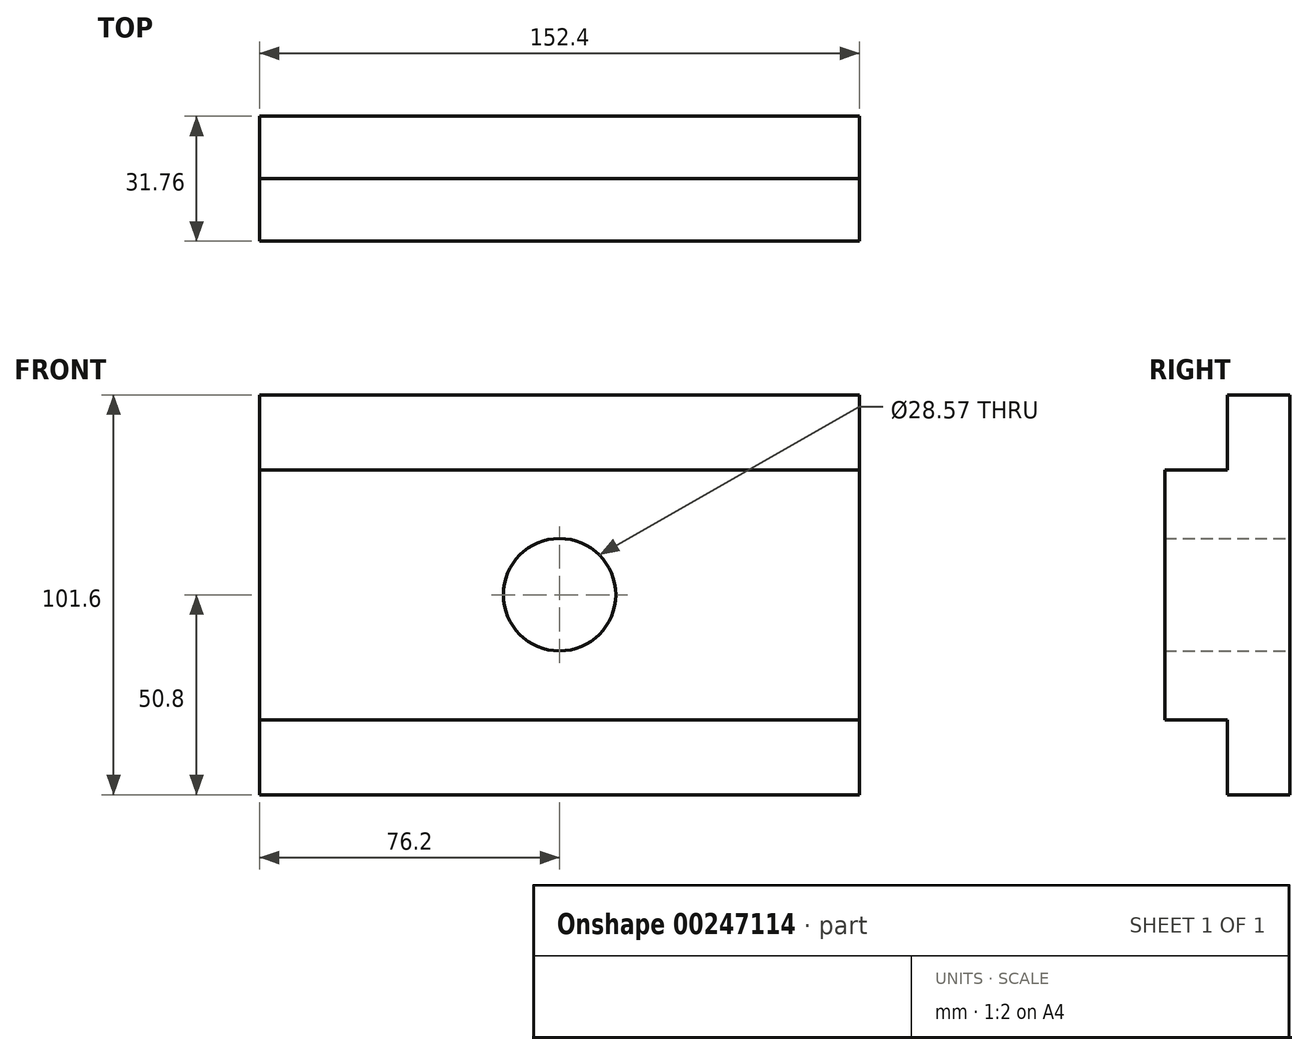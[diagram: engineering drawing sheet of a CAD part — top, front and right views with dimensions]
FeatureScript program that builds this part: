
annotation { "Feature Type Name" : "Feature", "Feature Type Description" : "" }
export const myFeature = defineFeature(function(context is Context, id is Id, definition is map)
    precondition{}
    {
        {
            var Q0;
            Q0=qCreatedBy(makeId("Front.planeOp"),FACE);
            var sketch = newSketch(context, id + "F0", { "sketchPlane" : qUnion([Q0])});
            skLineSegment(sketch, "E0.bottom", {"start": v(-76.2, 50.8) * mm, "end": v(76.2, 50.8) * mm});
            skLineSegment(sketch, "E0.top", {"start": v(-76.2, -50.8) * mm, "end": v(76.2, -50.8) * mm});
            skLineSegment(sketch, "E0.left", {"start": v(-76.2, 50.8) * mm, "end": v(-76.2, -50.8) * mm});
            skLineSegment(sketch, "E0.right", {"start": v(76.2, 50.8) * mm, "end": v(76.2, -50.8) * mm});
            skLineSegment(sketch, "E1.bottom", {"start": v(-76.2, 31.75) * mm, "end": v(76.2, 31.75) * mm});
            skLineSegment(sketch, "E1.top", {"start": v(-76.2, -31.75) * mm, "end": v(76.2, -31.75) * mm});
            skLineSegment(sketch, "E1.left", {"start": v(-76.2, 31.75) * mm, "end": v(-76.2, -31.75) * mm});
            skLineSegment(sketch, "E1.right", {"start": v(76.2, 31.75) * mm, "end": v(76.2, -31.75) * mm});
            skLineSegment(sketch, "E2", {"start": v(-76.2, -50.8) * mm, "end": v(-76.2, -31.75) * mm});
            skLineSegment(sketch, "E3", {"start": v(-76.2, 31.75) * mm, "end": v(-76.2, 50.8) * mm});
            skPoint(sketch, "E4", {"position": v(0, 0) * mm});
            skPoint(sketch, "E4.positionSnap0", {"position": v(-76.2, 0) * mm});
            skPoint(sketch, "E4.positionSnap1", {"position": v(0, 31.75) * mm});
            skCircle(sketch, "E5", {"center": v(0, 0) * mm, "radius": 14.29 * mm});
            skSolve(sketch);
        }
        {
            var Q0;
            Q0=makeQuery(id+"F0.imprint","IMPRINT",FACE,{"disambiguationData":[TD([[makeQuery(id+"F0.imprint","IMPRINT",EDGE,{"derivedFrom":sQuery(id+"F0.wireOp",EDGE,"E1.bottom")}),-1.0]])]});
            extrude(context, id + "F1", {"entities" : qUnion([Q0]), "depth" : 15.88 * mm});
        }
        {
            var Q0;
            Q0 = qSketchRegion(id + "F0", true);
            extrude(context, id + "F2", {"entities" : qUnion([Q0]), "operationType" : NewBodyOperationType.ADD, "oppositeDirection" : true, "depth" : 15.88 * mm});
        }
    });
